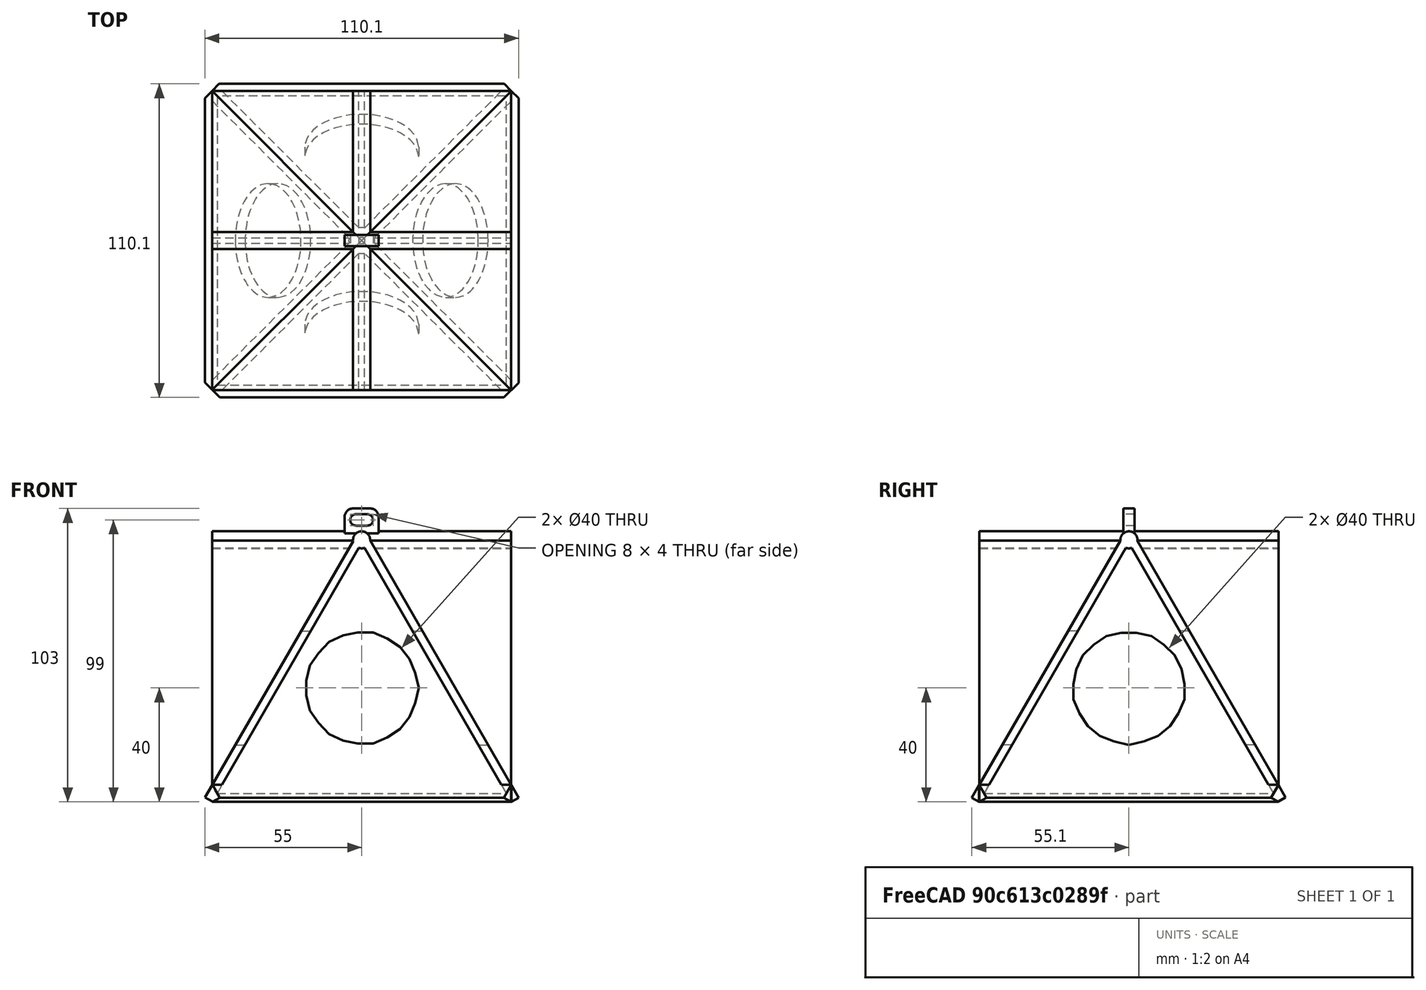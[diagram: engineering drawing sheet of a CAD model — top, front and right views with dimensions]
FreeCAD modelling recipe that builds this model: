
FCSTD DOCUMENT  (FreeCAD 0.18R4 (GitTag))
Label: birdhaus
License: All rights reserved
LicenseURL: http://en.wikipedia.org/wiki/All_rights_reserved
objects: Part::Box×12, Part::MultiFuse×7, Part::Cylinder×6, Part::Cut×3, Drawing::FeatureViewPart×2, Part::Fillet×1, Drawing::FeaturePage×1
note: 29 computed .brp shape members not serialized (recipe doc carries the construction recipe); baked Part::Feature solids carry a one-line shape summary decoded from their .brp

FEATURE [Part::Box] Box001  label="Cube001"
  AttacherType = Attacher::AttachEngine3D
  Height = 3
  Length = 105
  Width = 105
FEATURE [Part::Box] Box002  label="Cube002"
  AttacherType = Attacher::AttachEngine3D
  Height = 3
  Length = 105
  Placement = pos=(0,0,0) rot=(1,0,0;1.0472rad)
  Width = 105
FEATURE [Part::Box] Box003  label="Cube003"
  AttacherType = Attacher::AttachEngine3D
  Height = 3
  Length = 105
  Placement = pos=(0,52.4,91) rot=(1,0,0;-1.0472rad)
  Width = 105
FEATURE [Part::Cylinder] Cylinder
  Angle = 360
  AttacherType = Attacher::AttachEngine3D
  Height = 105
  Placement = pos=(0,52.5,92) rot=(0,1,0;1.5708rad)
  Radius = 3
FEATURE [Part::MultiFuse] Fusion
  Shapes = -> [Box001,Cylinder,Box003,Box002]
FEATURE [Part::Cylinder] Cylinder001
  Angle = 360
  AttacherType = Attacher::AttachEngine3D
  Height = 105
  Placement = pos=(0,52.5,92) rot=(0,1,0;1.5708rad)
  Radius = 3
FEATURE [Part::Box] Box004  label="Cube004"
  AttacherType = Attacher::AttachEngine3D
  Height = 3
  Length = 105
  Placement = pos=(0,52.4,91) rot=(-1,0,0;1.0472rad)
  Width = 105
FEATURE [Part::Box] Box005  label="Cube005"
  AttacherType = Attacher::AttachEngine3D
  Height = 3
  Length = 105
  Placement = pos=(0,0,0) rot=(1,0,0;1.0472rad)
  Width = 105
FEATURE [Part::Box] Box006  label="Cube006"
  AttacherType = Attacher::AttachEngine3D
  Height = 3
  Length = 105
  Width = 105
FEATURE [Part::MultiFuse] Fusion001
  Placement = pos=(105,0,0) rot=(0,0,1;1.5708rad)
  Shapes = -> [Box006,Cylinder001,Box004,Box005]
FEATURE [Part::MultiFuse] Fusion002  label="Shell"
  Shapes = -> [Fusion,Fusion001]
FEATURE [Part::Cylinder] Cylinder002
  Angle = 360
  AttacherType = Attacher::AttachEngine3D
  Height = 105
  Placement = pos=(52.5,105,40) rot=(1,0,0;1.5708rad)
  Radius = 20
FEATURE [Part::Cylinder] Cylinder003
  Angle = 360
  AttacherType = Attacher::AttachEngine3D
  Height = 105
  Placement = pos=(0,52.5,40) rot=(0,1,0;1.5708rad)
  Radius = 20
FEATURE [Part::MultiFuse] Fusion003
  Shapes = -> [Cylinder003,Cylinder002]
FEATURE [Part::Cut] Cut  label="House w/ Doors"
  Base = -> Fusion002
  Tool = -> Fusion003
FEATURE [Part::Box] Box  label="Cube"
  AttacherType = Attacher::AttachEngine3D
  Height = 12
  Length = 12
  Placement = pos=(46.5,50.5,91) rot=(0,0,1;0rad)
  Width = 4
FEATURE [Part::Fillet] Fillet
  Base = -> Box
  Edges = 2 edges r=3: [Edge2,Edge6]
FEATURE [Part::Box] Box007  label="Cube007"
  AttacherType = Attacher::AttachEngine3D
  Height = 10
  Length = 4
  Placement = pos=(0,-2,0) rot=(0,0,1;0rad)
  Width = 4
FEATURE [Part::Cylinder] Cylinder004
  Angle = 360
  AttacherType = Attacher::AttachEngine3D
  Height = 10
  Placement = pos=(4,0,0) rot=(0,0,1;0rad)
  Radius = 2
FEATURE [Part::Cylinder] Cylinder005
  Angle = 360
  AttacherType = Attacher::AttachEngine3D
  Height = 10
  Radius = 2
FEATURE [Part::MultiFuse] Fusion004
  Placement = pos=(50.5,57,99) rot=(1,0,0;1.5708rad)
  Shapes = -> [Box007,Cylinder005,Cylinder004]
FEATURE [Part::Cut] Cut001
  Base = -> Fillet
  Tool = -> Fusion004
FEATURE [Part::Box] Box008  label="Cube008"
  AttacherType = Attacher::AttachEngine3D
  Height = 10
  Length = 10
  Placement = pos=(-3,-11,0) rot=(0,0,1;0.785398rad)
  Width = 10
FEATURE [Part::Box] Box009  label="Cube009"
  AttacherType = Attacher::AttachEngine3D
  Height = 10
  Length = 10
  Placement = pos=(-3,102,0) rot=(0,0,1;0.785398rad)
  Width = 10
FEATURE [Part::Box] Box010  label="Cube010"
  AttacherType = Attacher::AttachEngine3D
  Height = 10
  Length = 10
  Placement = pos=(108.2,-11,0) rot=(0,0,1;0.785398rad)
  Width = 10
FEATURE [Part::Box] Box011  label="Cube011"
  AttacherType = Attacher::AttachEngine3D
  Height = 10
  Length = 10
  Placement = pos=(108.2,101.8,0) rot=(0,0,1;0.785398rad)
  Width = 10
FEATURE [Part::MultiFuse] Fusion005
  Shapes = -> [Box009,Box008,Box010,Box011]
FEATURE [Part::Cut] Cut002
  Base = -> Cut
  Tool = -> Fusion005
FEATURE [Part::MultiFuse] Fusion006  label="birdhaus-draft"
  Shapes = -> [Cut001,Cut002]
FEATURE [Drawing::FeatureViewPart] Ortho  label="Ortho_0_0"
  Direction = (1,0,0)
  HiddenWidth = 0.15
  LineWidth = 0.35
  Rotation = -90
  Scale = 1.5
  ShowHiddenLines = false
  ShowSmoothLines = false
  Source = -> Fusion006
  Tolerance = 0.05
  ViewResult = <blob: 4528 chars omitted>
  Visible = false
  X = 101.801
  Y = 383.215
FEATURE [Drawing::FeatureViewPart] Ortho001  label="Ortho_1_1"
  Direction = (0.57735,0.57735,0.57735)
  HiddenWidth = 0.15
  LineWidth = 0.35
  Rotation = 120
  Scale = 1.5
  ShowHiddenLines = false
  ShowSmoothLines = false
  Source = -> Fusion006
  Tolerance = 0.05
  ViewResult = <blob: 10049 chars omitted>
  Visible = false
  X = 423.63
  Y = 118.133
FEATURE [Drawing::FeaturePage] Page
  EditableTexts = AUTHOR NAME | DRAWING TITLE | FreeCAD DRAWING | A2 | X / Y | SCALE | PN | DN | DD/MM/YYYY | REV A
  Group = -> [Ortho,Ortho001]
  Template = C:/Program Files/FreeCAD 0.18/data/Mod/Drawing/Templates/A2_Landscape_ISO7200.svg
